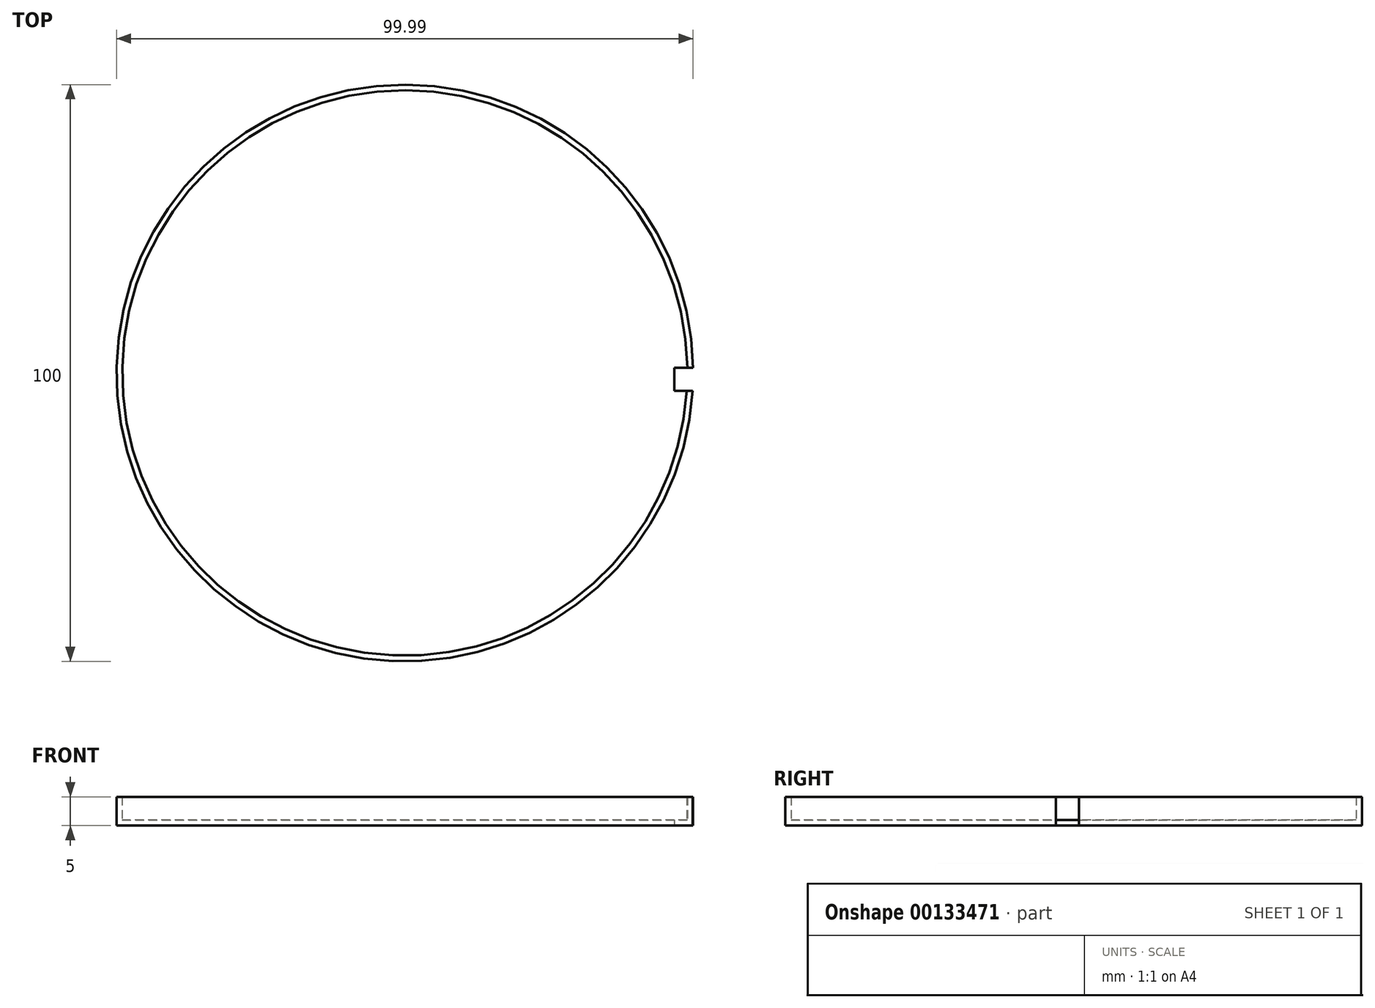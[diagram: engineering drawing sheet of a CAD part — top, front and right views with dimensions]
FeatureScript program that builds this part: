
annotation { "Feature Type Name" : "Feature", "Feature Type Description" : "" }
export const myFeature = defineFeature(function(context is Context, id is Id, definition is map)
    precondition{}
    {
        {
            var Q0;
            Q0=qCreatedBy(makeId("Top.planeOp"),FACE);
            var sketch = newSketch(context, id + "F0", { "sketchPlane" : qUnion([Q0])});
            skCircle(sketch, "E0", {"center": v(0, 0) * mm, "radius": 50 * mm});
            skSolve(sketch);
        }
        {
            var Q0;
            Q0=makeQuery(id+"F0.imprint","IMPRINT",FACE,{"disambiguationData":[TD([[makeQuery(id+"F0.imprint","IMPRINT",EDGE,{"derivedFrom":sQuery(id+"F0.wireOp",EDGE,"E0")}),1.0]])]});
            extrude(context, id + "F1", {"entities" : qUnion([Q0]), "depth" : 5 * mm});
        }
        {
            var Q0;
            Q0=makeQuery(id+"F1.opExtrude","CAP_FACE",FACE,{"disambiguationData":[OSD([sQuery(id+"F0.wireOp",EDGE,"E0")])],"isStart":false});
            shell(context, id + "F2", {"entities" : qUnion([Q0]), "thickness" : 1 * mm});
        }
        {
            var Q0;
            Q0=qCreatedBy(makeId("Top.planeOp"),FACE);
            var sketch = newSketch(context, id + "F3", { "sketchPlane" : qUnion([Q0])});
            skLineSegment(sketch, "E1.bottom", {"start": v(46.7, 0.9) * mm, "end": v(50.7, 0.9) * mm});
            skLineSegment(sketch, "E1.top", {"start": v(46.7, -3.1) * mm, "end": v(50.7, -3.1) * mm});
            skLineSegment(sketch, "E1.left", {"start": v(46.7, 0.9) * mm, "end": v(46.7, -3.1) * mm});
            skLineSegment(sketch, "E1.right", {"start": v(50.7, 0.9) * mm, "end": v(50.7, -3.1) * mm});
            skSolve(sketch);
        }
        {
            var Q0;
            Q0=makeQuery(id+"F3.imprint","IMPRINT",FACE,{"disambiguationData":[TD([[makeQuery(id+"F3.imprint","IMPRINT",EDGE,{"derivedFrom":sQuery(id+"F3.wireOp",EDGE,"E1.bottom")}),-1.0]])]});
            extrude(context, id + "F4", {"entities" : qUnion([Q0]), "operationType" : NewBodyOperationType.REMOVE, "depth" : 6 * mm});
        }
        {
            var Q0;
            Q0=qCreatedBy(makeId("Top.planeOp"),FACE);
            var sketch = newSketch(context, id + "F5", { "sketchPlane" : qUnion([Q0])});
            skCircle(sketch, "E2", {"center": v(0, 0) * mm, "radius": 1.6 * mm});
            skSolve(sketch);
        }
        {
            var Q0;
            Q0=sQuery(id+"F5.wireOp",EDGE,"E2");
            extrude(context, id + "F6", {"bodyType" : ToolBodyType.SURFACE, "surfaceEntities" : qUnion([Q0]), "depth" : 5 * mm});
        }
    });
